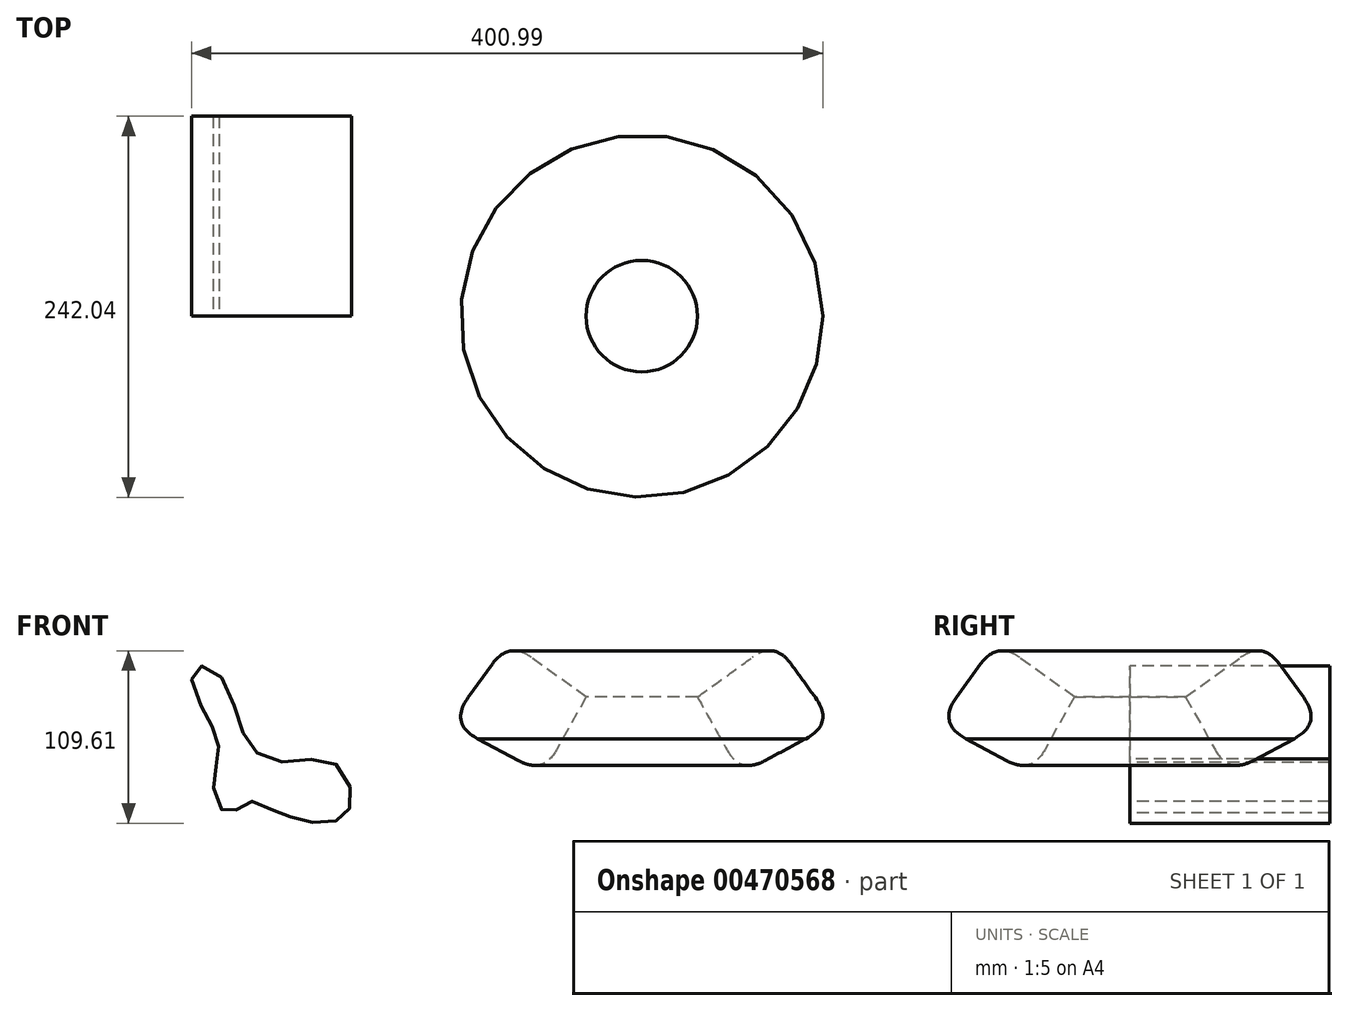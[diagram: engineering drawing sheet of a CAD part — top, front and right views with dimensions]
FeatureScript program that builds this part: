
annotation { "Feature Type Name" : "Feature", "Feature Type Description" : "" }
export const myFeature = defineFeature(function(context is Context, id is Id, definition is map)
    precondition{}
    {
        {
            var Q0;
            Q0=qCreatedBy(makeId("Front.planeOp"),FACE);
            var sketch = newSketch(context, id + "F0", { "sketchPlane" : qUnion([Q0])});
            skFitSpline(sketch, "E0", {"points": [v(-58.52, 26.01) * mm, v(-63.9, 48.63) * mm, v(-51.46, 49.76) * mm, v(-36.75, 23.47) * mm, v(-26.86, 0) * mm, v(-4.8, -9.61) * mm, v(23.47, -8.76) * mm, v(36.47, -28.27) * mm, v(33.93, -41.84) * mm, v(20.64, -48.35) * mm, v(0, -44.95) * mm, v(-11.03, -41) * mm, v(-27.7, -34.5) * mm, v(-37.88, -41) * mm, v(-46.08, -39.3) * mm, v(-50.89, -20.36) * mm, v(-47.5, -6.22) * mm, v(-50.04, 9.9) * mm, v(-58.52, 26.01) * mm]});
            skSolve(sketch);
        }
        {
            var Q0;
            Q0 = qSketchRegion(id + "F0", true);
            extrude(context, id + "F1", {"entities" : qUnion([Q0]), "oppositeDirection" : true, "depth" : 127 * mm});
        }
        {
            var Q0;
            Q0=qCreatedBy(makeId("Front.planeOp"),FACE);
            var sketch = newSketch(context, id + "F2", { "sketchPlane" : qUnion([Q0])});
            skLineSegment(sketch, "E1", {"start": v(158.55, -16.97) * mm, "end": v(99, 14.94) * mm});
            skLineSegment(sketch, "E2", {"start": v(99, 14.94) * mm, "end": v(136.73, 67.23) * mm});
            skLineSegment(sketch, "E3", {"start": v(136.73, 67.23) * mm, "end": v(185.83, 31.8) * mm});
            skLineSegment(sketch, "E4", {"start": v(185.83, 31.8) * mm, "end": v(158.55, -16.97) * mm});
            skLineSegment(sketch, "E5", {"start": v(221.18, 84.95) * mm, "end": v(221.18, -67.77) * mm});
            skSolve(sketch);
        }
        {
            var Q0;
            Q0 = qSketchRegion(id + "F2", true);
            var Q1;
            Q1=sQuery(id+"F2.wireOp",EDGE,"E5");
            revolve(context, id + "F3", {"entities" : qUnion([Q0]), "axis" : qUnion([Q1]), "revolveType" : RevolveType.FULL});
        }
        {
            var Q0;
            Q0=makeQuery(id+"F3.opRevolve","SWEPT_EDGE",EDGE,{"disambiguationData":[OSD([sQuery(id+"F2.wireOp",EDGE,"E2"),sQuery(id+"F2.wireOp",EDGE,"E3")])]});
            var Q1;
            Q1=makeQuery(id+"F3.opRevolve","SWEPT_EDGE",EDGE,{"disambiguationData":[OSD([sQuery(id+"F2.wireOp",EDGE,"E1"),sQuery(id+"F2.wireOp",EDGE,"E2")])]});
            var Q2;
            Q2=makeQuery(id+"F3.opRevolve","SWEPT_EDGE",EDGE,{"disambiguationData":[OSD([sQuery(id+"F2.wireOp",EDGE,"E1"),sQuery(id+"F2.wireOp",EDGE,"E4")])]});
            fillet(context, id + "F4", {"entities" : qUnion([Q0, Q1, Q2]), "radius" : 17.78 * mm, "tangentPropagation" : true, "rho" : 0.5, "crossSection" : FilletCrossSection.CONIC, "allowEdgeOverflow" : false});
        }
    });
